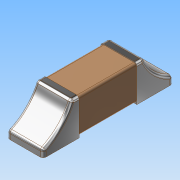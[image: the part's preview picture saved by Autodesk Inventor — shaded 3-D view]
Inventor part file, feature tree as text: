
AUTODESK INVENTOR PART (.ipt)
format: ipt  version: 2016 (Build 200138000, 138)  size: 195,072 bytes
history: native  units: mm
features: extrude x3, fillet x3, sketch x2, mirror x1, projected_geometry x1
ambient origin geometry x8: Origin, YZ Plane, XZ Plane, XY Plane, X Axis, Y Axis, Z Axis, Center Point
bodies: Body1 (feature_tree)
feature tree (10):
  extrude  "Extrusion4"  Depth=0.475mm
  sketch  "Sketch11"  dims[d9=0.475mm d10=0.0mm d11=0.5mm d12=0.1mm d13=0.0mm d14=0.1mm d15=0.5mm d16=0.0mm d17=0.75mm d18=0.0425mm d19=0.03mm]
  extrude  "Extrusion5"  Depth=0.5mm
  extrude  "Extrusion6"  Depth=0.03mm TaperAngle=0.0deg
  fillet  "Fillet1"  Radius=0.1mm
  fillet  "Fillet2"  Radius=0.5mm
  mirror  "Mirror1"
  fillet  "Fillet3"  Radius=0.75mm
  sketch  "Sketch10"  dims[d7=0.8mm d8=0.475mm]
  projected_geometry  "Projected Loop1"
